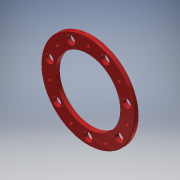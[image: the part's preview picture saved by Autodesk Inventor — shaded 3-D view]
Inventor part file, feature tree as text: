
AUTODESK INVENTOR PART (.ipt)
format: ipt  version: 2018 (Build 220112000, 112)  size: 161,792 bytes
history: native  units: mm
features: extrude x1, fillet x1, sketch x1
ambient origin geometry x8: Origin, YZ Plane, XZ Plane, XY Plane, X Axis, Y Axis, Z Axis, Center Point
bodies: Solid1 (feature_tree)
feature tree (3):
  extrude  "Extrusion1"  Depth=1.0mm
  fillet  "Fillet1"  Radius=110.0mm
  sketch  "Sketch1"  dims[d0=90.0mm d1=130.0mm d2=110.0mm d3=12.0mm d4=5.0mm d5=70.0mm d7=360.0deg d9=6.0mm d10=0.0mm d11=1.0mm]
